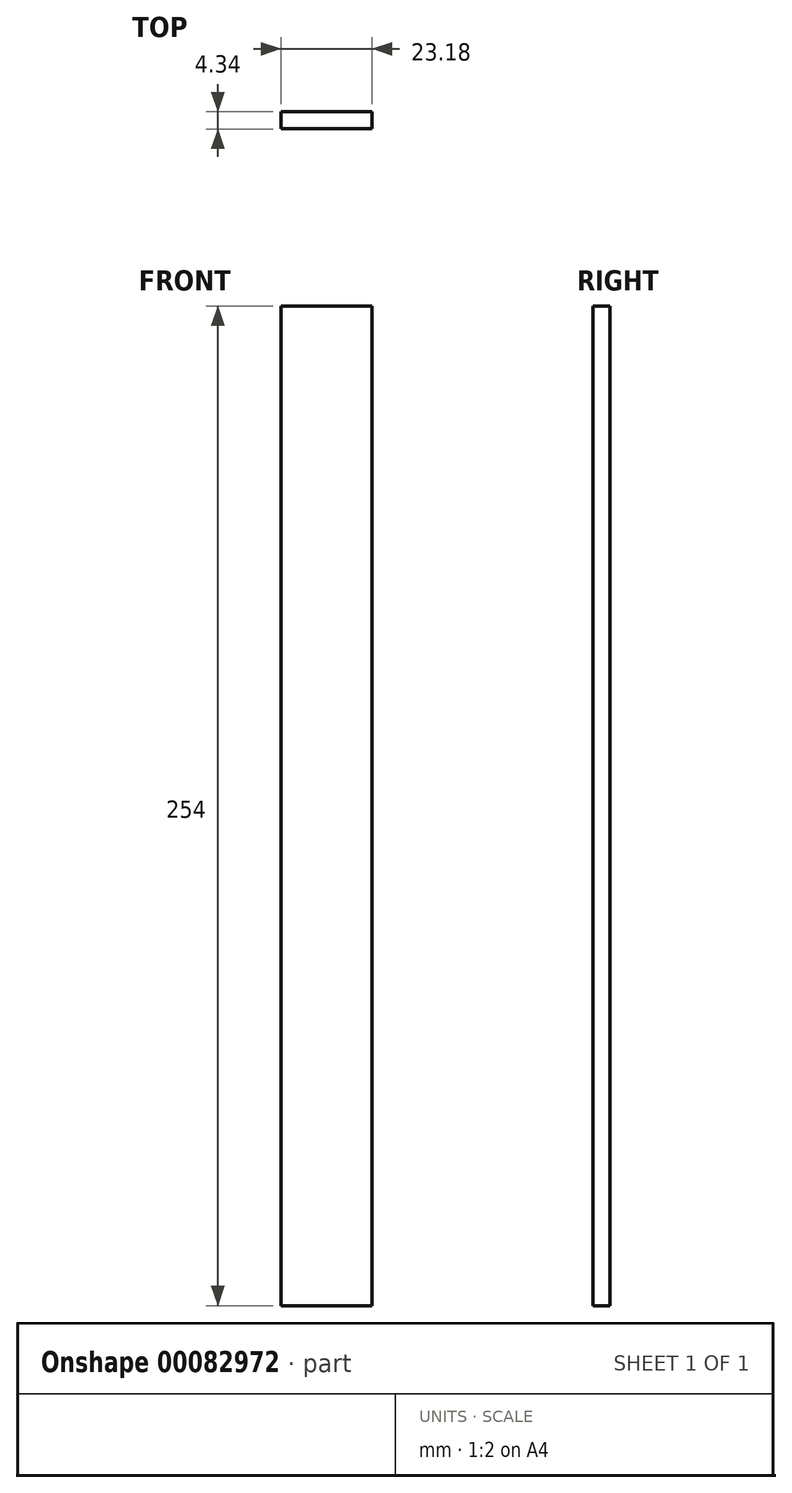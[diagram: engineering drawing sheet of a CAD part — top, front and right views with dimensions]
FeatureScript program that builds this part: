
annotation { "Feature Type Name" : "Feature", "Feature Type Description" : "" }
export const myFeature = defineFeature(function(context is Context, id is Id, definition is map)
    precondition{}
    {
        {
            var Q0;
            Q0=qCreatedBy(makeId("Top.planeOp"),FACE);
            var sketch = newSketch(context, id + "F0", { "sketchPlane" : qUnion([Q0])});
            skLineSegment(sketch, "E0.bottom", {"start": v(-55.32, 44.2) * mm, "end": v(-32.14, 44.2) * mm});
            skLineSegment(sketch, "E0.top", {"start": v(-55.32, 39.86) * mm, "end": v(-32.14, 39.86) * mm});
            skLineSegment(sketch, "E0.left", {"start": v(-55.32, 44.2) * mm, "end": v(-55.32, 39.86) * mm});
            skLineSegment(sketch, "E0.right", {"start": v(-32.14, 44.2) * mm, "end": v(-32.14, 39.86) * mm});
            skSolve(sketch);
        }
        {
            var Q0;
            Q0=makeQuery(id+"F0.imprint","IMPRINT",FACE,{"disambiguationData":[TD([[makeQuery(id+"F0.imprint","IMPRINT",EDGE,{"derivedFrom":sQuery(id+"F0.wireOp",EDGE,"E0.bottom")}),-1.0]])]});
            extrude(context, id + "F1", {"entities" : qUnion([Q0]), "depth" : 254 * mm});
        }
    });
